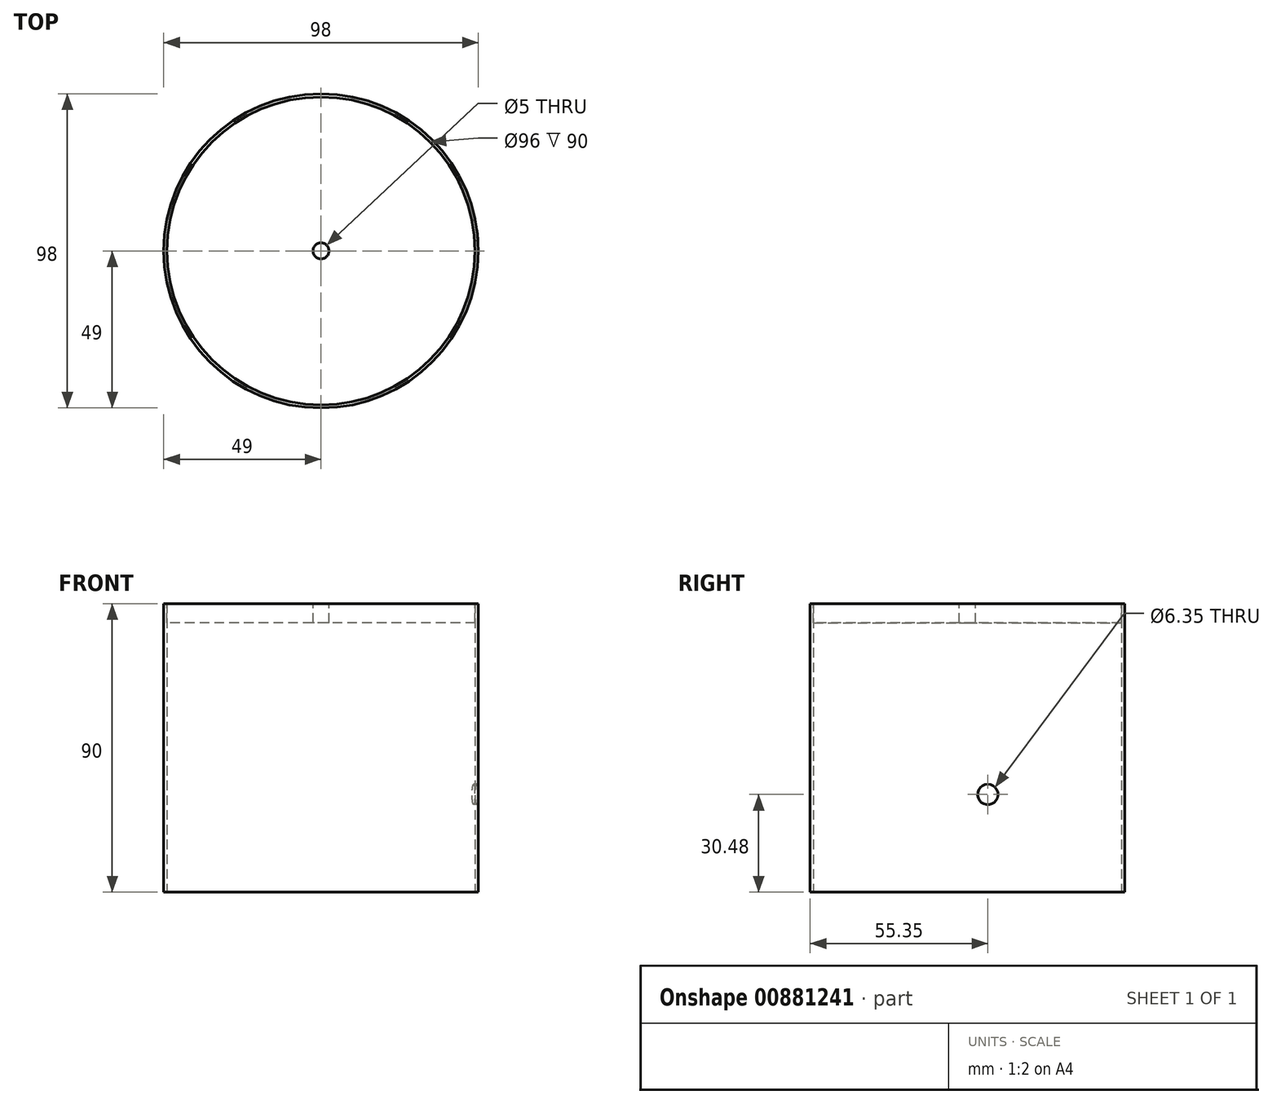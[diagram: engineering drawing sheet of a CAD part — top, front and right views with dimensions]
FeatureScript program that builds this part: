
annotation { "Feature Type Name" : "Feature", "Feature Type Description" : "" }
export const myFeature = defineFeature(function(context is Context, id is Id, definition is map)
    precondition{}
    {
        {
            var Q0;
            Q0=qCreatedBy(makeId("Top.planeOp"),FACE);
            var sketch = newSketch(context, id + "F0", { "sketchPlane" : qUnion([Q0])});
            skCircle(sketch, "E0", {"center": v(0, 0) * mm, "radius": 49 * mm});
            skCircle(sketch, "E1", {"center": v(0, 0) * mm, "radius": 48 * mm});
            skSolve(sketch);
        }
        {
            var Q0;
            Q0=qSketchRegion(id+"F0",true);
            extrude(context, id + "F1", {"entities" : qUnion([Q0]), "depth" : 90 * mm, "offsetDistance" : 25.4 * mm});
        }
        {
            var Q0;
            Q0=makeQuery(id+"F1.opExtrude","CAP_FACE",FACE,{"disambiguationData":[OSD([sQuery(id+"F0.wireOp",EDGE,"E0"),sQuery(id+"F0.wireOp",EDGE,"E1")])],"isStart":false});
            var sketch = newSketch(context, id + "F2", { "sketchPlane" : qUnion([Q0])});
            skCircle(sketch, "E2", {"center": v(0, 0) * mm, "radius": 48 * mm});
            skCircle(sketch, "E3", {"center": v(0, 0) * mm, "radius": 2.5 * mm});
            skSolve(sketch);
        }
        {
            var Q0;
            Q0=qSketchRegion(id+"F2",true);
            extrude(context, id + "F3", {"entities" : qUnion([Q0]), "oppositeDirection" : true, "depth" : 6 * mm, "offsetDistance" : 25.4 * mm});
        }
        {
            var Q0;
            Q0=qCreatedBy(makeId("Right.planeOp"),FACE);
            var sketch = newSketch(context, id + "F4", { "sketchPlane" : qUnion([Q0])});
            skCircle(sketch, "E4", {"center": v(6.35, 30.48) * mm, "radius": 3.18 * mm});
            skSolve(sketch);
        }
        {
            var Q0;
            Q0=qSketchRegion(id+"F4",true);
            extrude(context, id + "F5", {"entities" : qUnion([Q0]), "operationType" : NewBodyOperationType.REMOVE, "depth" : 127 * mm, "offsetDistance" : 25.4 * mm});
        }
    });
